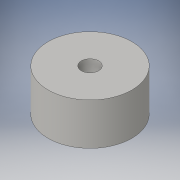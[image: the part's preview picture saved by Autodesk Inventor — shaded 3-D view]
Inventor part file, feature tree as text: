
AUTODESK INVENTOR PART (.ipt)
format: ipt  version: 2016 (Build 200138000, 138)  size: 89,088 bytes
history: native  units: in
note: dims shown in document units (in); Inventor stores cm internally (conversion verified against a paired STEP export)
features: extrude x1, sketch x1
ambient origin geometry x8: Origin, YZ Plane, XZ Plane, XY Plane, X Axis, Y Axis, Z Axis, Center Point
bodies: Solid1 (feature_tree)
feature tree (2):
  extrude  "Extrusion1"  Depth=2.0in
  sketch  "Sketch1"  dims[d0=0.8268in d1=4.0in d2=2.0in d3=0.0in]
